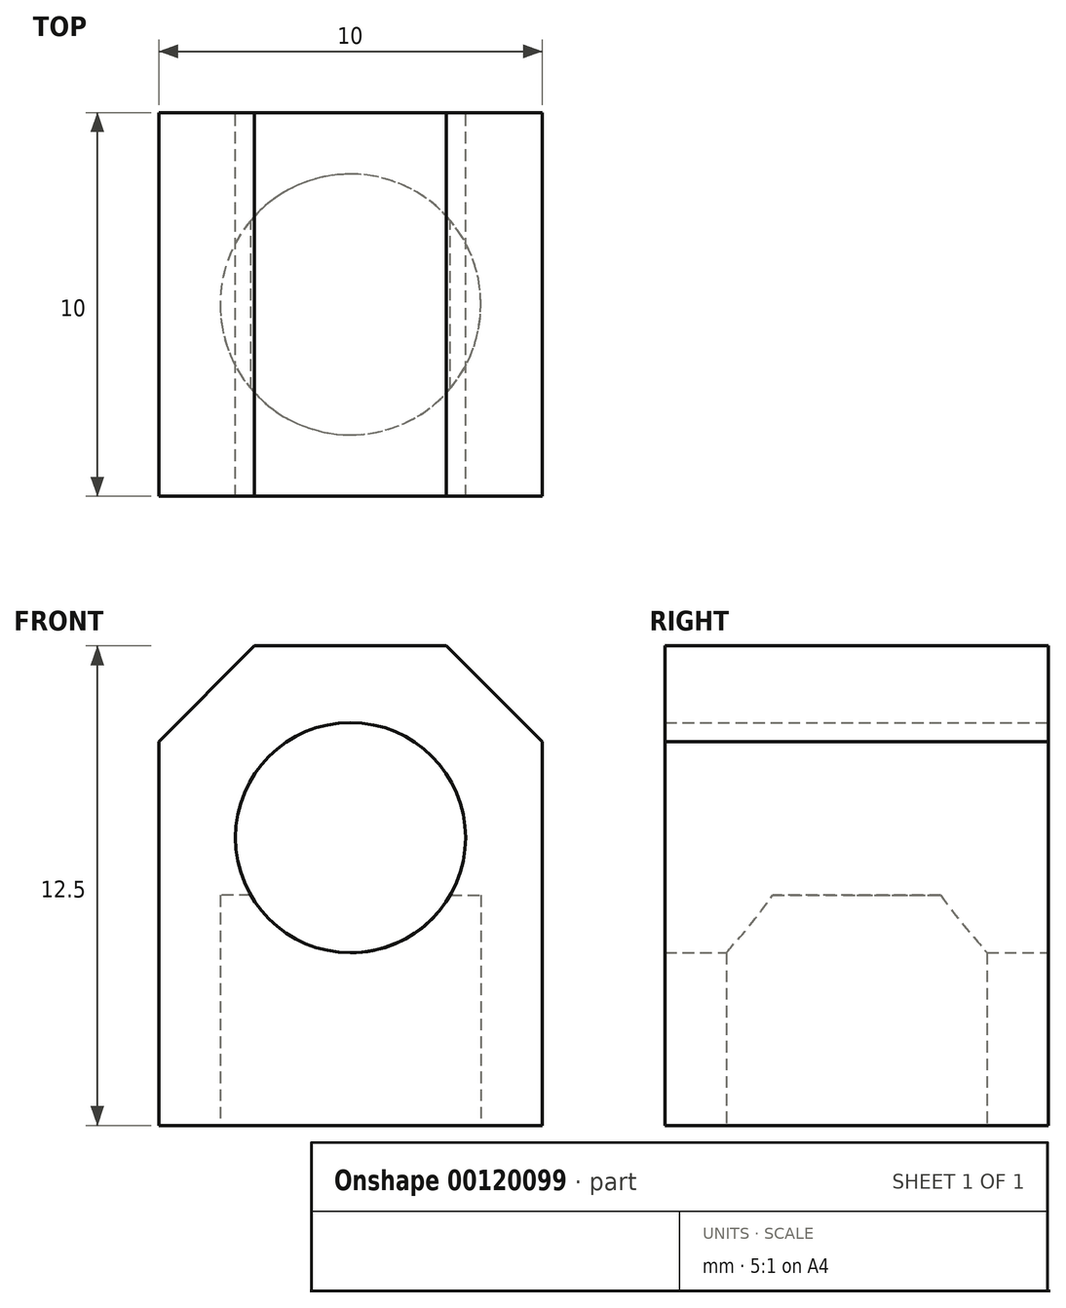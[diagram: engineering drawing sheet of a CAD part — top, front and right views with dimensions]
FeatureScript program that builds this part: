
annotation { "Feature Type Name" : "Feature", "Feature Type Description" : "" }
export const myFeature = defineFeature(function(context is Context, id is Id, definition is map)
    precondition{}
    {
        {
            var Q0;
            Q0=qCreatedBy(makeId("Front.planeOp"),FACE);
            var sketch = newSketch(context, id + "F0", { "sketchPlane" : qUnion([Q0])});
            skCircle(sketch, "E0", {"center": v(0, 0) * mm, "radius": 3 * mm});
            skLineSegment(sketch, "E1.top", {"start": v(-5, 5) * mm, "end": v(5, 5) * mm});
            skLineSegment(sketch, "E1.left", {"start": v(-5, -5) * mm, "end": v(-5, 5) * mm});
            skLineSegment(sketch, "E1.right", {"start": v(5, -5) * mm, "end": v(5, 5) * mm});
            skLineSegment(sketch, "E2", {"start": v(-5, -5) * mm, "end": v(-5, -7.5) * mm});
            skLineSegment(sketch, "E3", {"start": v(5, -5) * mm, "end": v(5, -7.5) * mm});
            skLineSegment(sketch, "E4", {"start": v(5, -7.5) * mm, "end": v(-5, -7.5) * mm});
            skSolve(sketch);
        }
        {
            var Q0;
            Q0 = qSketchRegion(id + "F0", true);
            extrude(context, id + "F1", {"entities" : qUnion([Q0]), "endBound" : BoundingType.SYMMETRIC, "depth" : 10 * mm});
        }
        {
            var Q0;
            Q0=makeQuery(id+"F1.opExtrude","SWEPT_FACE",FACE,{"disambiguationData":[OSD([sQuery(id+"F0.wireOp",EDGE,"E4")])]});
            var sketch = newSketch(context, id + "F2", { "sketchPlane" : qUnion([Q0])});
            skCircle(sketch, "E5", {"center": v(0, 0) * mm, "radius": 3.4 * mm});
            skSolve(sketch);
        }
        {
            var Q0;
            Q0=makeQuery(id+"F2.imprint","IMPRINT",FACE,{"disambiguationData":[TD([[makeQuery(id+"F2.imprint","IMPRINT",EDGE,{"derivedFrom":sQuery(id+"F2.wireOp",EDGE,"E5")}),1.0]])]});
            extrude(context, id + "F3", {"entities" : qUnion([Q0]), "operationType" : NewBodyOperationType.REMOVE, "oppositeDirection" : true, "depth" : 6 * mm});
        }
        {
            var Q0;
            Q0=makeQuery(id+"F1.opExtrude","SWEPT_EDGE",EDGE,{"disambiguationData":[OSD([sQuery(id+"F0.wireOp",EDGE,"E1.top"),sQuery(id+"F0.wireOp",EDGE,"E1.left")])]});
            var Q1;
            Q1=makeQuery(id+"F1.opExtrude","SWEPT_EDGE",EDGE,{"disambiguationData":[OSD([sQuery(id+"F0.wireOp",EDGE,"E1.top"),sQuery(id+"F0.wireOp",EDGE,"E1.right")])]});
            chamfer(context, id + "F4", {"entities" : qUnion([Q0, Q1]), "width" : 2.5 * mm, "tangentPropagation" : true});
        }
    });
